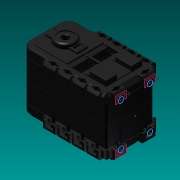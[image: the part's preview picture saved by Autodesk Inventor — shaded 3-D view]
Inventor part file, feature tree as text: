
AUTODESK INVENTOR PART (.ipt)
format: ipt  version: 2013 SP2 (Build 170200200, 200)  size: 2,207,232 bytes
history: native  units: in
note: dims shown in document units (in); Inventor stores cm internally (conversion verified against a paired STEP export)
features: projected_geometry x3, imported_body x1, sketch x1
ambient origin geometry x8: Origin, YZ Plane, XZ Plane, XY Plane, X Axis, Y Axis, Z Axis, Center Point
bodies: Solid1 (feature_tree)
feature tree (5):
  imported_body  "Base1"
  sketch  "Sketch1"  dims[d0=0.1181in d1=0.1181in d2=0.1181in d3=0.1181in]
  projected_geometry  "Projected Loop1"
  projected_geometry  "Projected Loop2"
  projected_geometry  "Projected Loop3"
